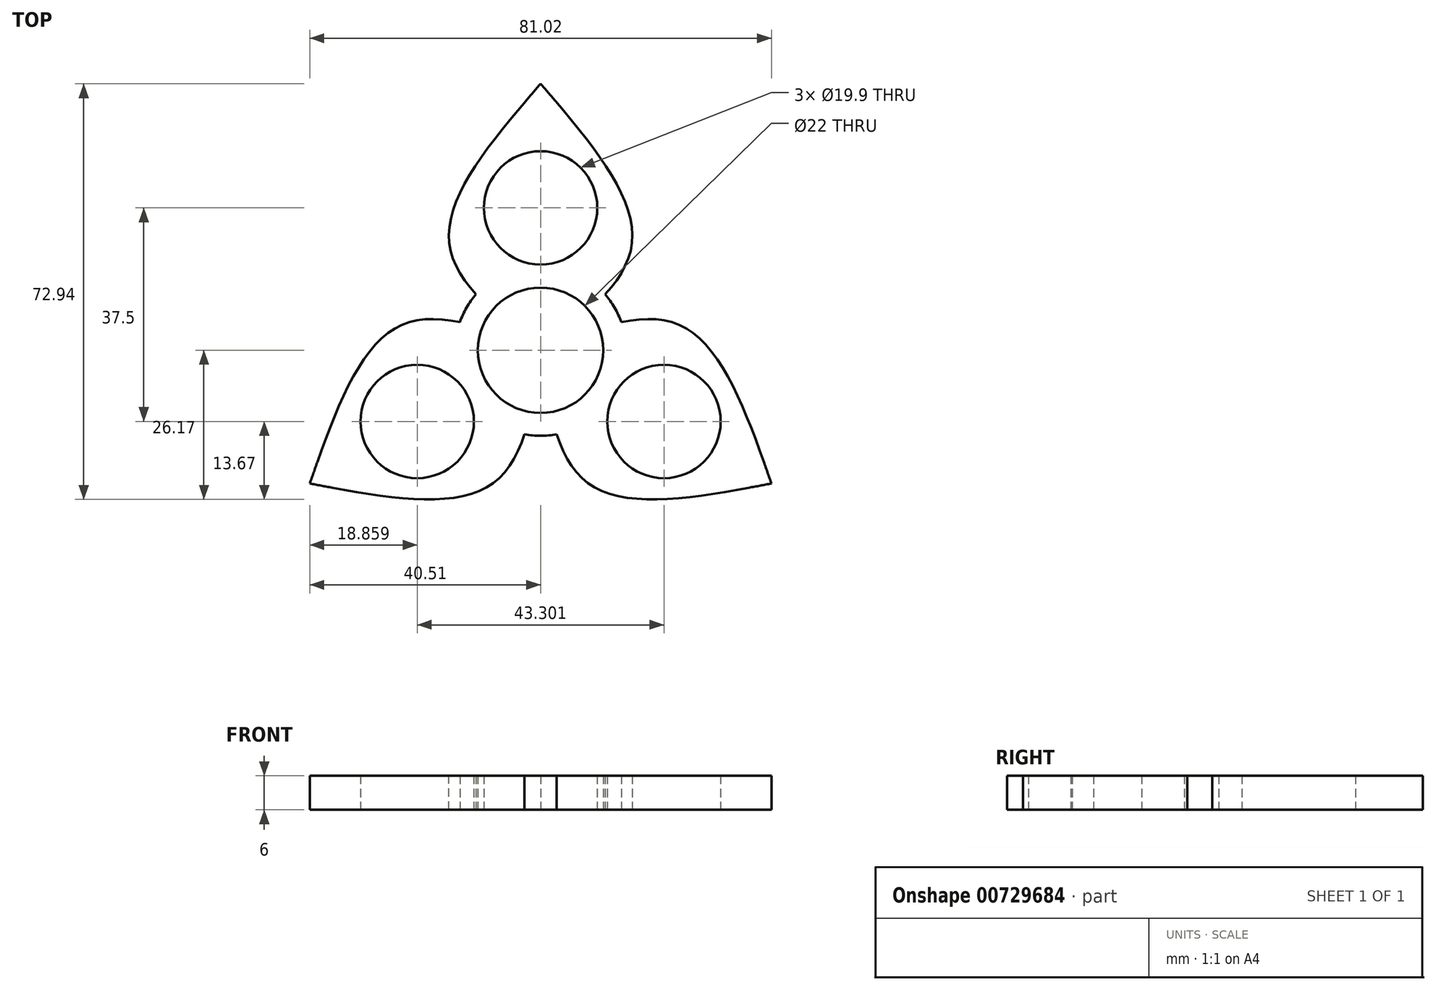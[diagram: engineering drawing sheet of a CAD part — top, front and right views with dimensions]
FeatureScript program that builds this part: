
annotation { "Feature Type Name" : "Feature", "Feature Type Description" : "" }
export const myFeature = defineFeature(function(context is Context, id is Id, definition is map)
    precondition{}
    {
        {
            var Q0;
            Q0=qCreatedBy(makeId("Top.planeOp"),FACE);
            var sketch = newSketch(context, id + "F0", { "sketchPlane" : qUnion([Q0])});
            skArc(sketch, "E0", {"start": v(11, 0) * mm, "mid": v(0, 11) * mm, "end": v(-11, 0) * mm});
            skArc(sketch, "E1", {"start": v(14.17, 4.92) * mm, "mid": v(13, 7.5) * mm, "end": v(11.35, 9.81) * mm});
            skLineSegment(sketch, "E2", {"start": v(0, 15) * mm, "end": v(0, 15.05) * mm});
            skCircle(sketch, "E3", {"center": v(0, 25) * mm, "radius": 9.95 * mm});
            skFitSpline(sketch, "E4", {"points": [v(0, 0) * mm, v(-16.07, 19.15) * mm, v(0, 46.77) * mm], "startDerivative": vector(-49.38, 38.16) * mm, "endDerivative": vector(47.4, 55.04) * mm});
            skFitSpline(sketch, "E5", {"points": [v(0, 0) * mm, v(16.07, 19.15) * mm, v(0, 46.77) * mm], "startDerivative": vector(49.38, 38.16) * mm, "endDerivative": vector(-47.4, 55.04) * mm});
            skFitSpline(sketch, "E6", {"points": [v(-2.6, 43.74) * mm, v(0, 39.95) * mm, v(2.6, 43.74) * mm], "startDerivative": vector(5.21, -11.36) * mm, "endDerivative": vector(5.21, 11.36) * mm});
            skArc(sketch, "E7.1.1", {"start": v(-11.35, 9.81) * mm, "mid": v(-13, 7.5) * mm, "end": v(-14.17, 4.92) * mm});
            skArc(sketch, "E7.2.2", {"start": v(7.07, 8.43) * mm, "mid": v(6.3, 9.01) * mm, "end": v(5.5, 9.53) * mm});
            skArc(sketch, "E8.1.0", {"start": v(-5.5, 9.53) * mm, "mid": v(-9.53, -5.5) * mm, "end": v(5.5, -9.53) * mm});
            skArc(sketch, "E8.1.3", {"start": v(-2.82, -14.73) * mm, "mid": v(0, -15) * mm, "end": v(2.82, -14.73) * mm});
            skCircle(sketch, "E8.1.4", {"center": v(-21.65, -12.5) * mm, "radius": 9.95 * mm});
            skArc(sketch, "E8.2.0", {"start": v(-5.5, -9.53) * mm, "mid": v(9.53, -5.5) * mm, "end": v(5.5, 9.53) * mm});
            skArc(sketch, "E8.2.1", {"start": v(-2.82, -14.73) * mm, "mid": v(0, -15) * mm, "end": v(2.82, -14.73) * mm});
            skArc(sketch, "E8.2.2", {"start": v(-2.82, -14.73) * mm, "mid": v(0, -15) * mm, "end": v(2.82, -14.73) * mm});
            skCircle(sketch, "E8.2.4", {"center": v(21.65, -12.5) * mm, "radius": 9.95 * mm});
            skLineSegment(sketch, "E9.trimOffspring", {"start": v(0, 15.05) * mm, "end": v(0, 15) * mm});
            skLineSegment(sketch, "E10.trimOffspring", {"start": v(13, -7.5) * mm, "end": v(13.03, -7.52) * mm});
            skFitSpline(sketch, "E11.MirrorCS", {"points": [v(0, 0) * mm, v(24.62, 4.34) * mm, v(40.5, -23.39) * mm], "startDerivative": vector(57.74, 23.68) * mm, "endDerivative": vector(23.96, -68.57) * mm});
            skFitSpline(sketch, "E12.MirrorCS", {"points": [v(36.57, -24.12) * mm, v(34.6, -19.98) * mm, v(39.18, -19.61) * mm], "startDerivative": vector(-7.23, 10.2) * mm, "endDerivative": vector(12.44, -1.17) * mm});
            skFitSpline(sketch, "E13.MirrorCS", {"points": [v(36.57, -24.12) * mm, v(34.6, -19.98) * mm, v(39.18, -19.61) * mm], "startDerivative": vector(-7.23, 10.2) * mm, "endDerivative": vector(12.44, -1.17) * mm});
            skFitSpline(sketch, "E14.MirrorCS", {"points": [v(0, 0) * mm, v(8.55, -23.5) * mm, v(40.5, -23.39) * mm], "startDerivative": vector(8.36, -61.85) * mm, "endDerivative": vector(71.36, 13.53) * mm});
            skFitSpline(sketch, "E15.MirrorCS", {"points": [v(0, 0) * mm, v(-24.62, 4.34) * mm, v(-40.5, -23.39) * mm], "startDerivative": vector(-57.74, 23.68) * mm, "endDerivative": vector(-23.96, -68.57) * mm});
            skFitSpline(sketch, "E16.MirrorCS", {"points": [v(-39.18, -19.61) * mm, v(-34.6, -19.97) * mm, v(-36.57, -24.12) * mm], "startDerivative": vector(12.44, 1.17) * mm, "endDerivative": vector(-7.23, -10.2) * mm});
            skFitSpline(sketch, "E17.MirrorCS", {"points": [v(0, 0) * mm, v(-8.55, -23.5) * mm, v(-40.5, -23.39) * mm], "startDerivative": vector(-8.36, -61.85) * mm, "endDerivative": vector(-71.36, 13.53) * mm});
            skSolve(sketch);
        }
        {
            var Q0;
            Q0 = qSketchRegion(id + "F0", true);
            extrude(context, id + "F1", {"entities" : qUnion([Q0]), "depth" : 6 * mm, "offsetDistance" : 25 * mm});
        }
    });
